# Revit family: Sanitary-Equipment_Urinal-Bill_085135
name_source: partatom
category: Plumbing Fixtures
revit_build: Autodesk Revit 2014 (Build: 20130308_1515(x64)
units: mm (PartAtom-declared; Revit-internal decimal feet)

## types (1)
- 085135 White Alpin
    BIMobject category = Urinals
    Depth (mm) = 355 mm
    Description = Urinal concealed inlet, syphonic action, vertical or horizontal outlet
    Drain Diameter (mm) = 50 mm  [stored 0.164042 ft]
    Edition number = 1
    Height (mm) = 510 mm  [stored 1.67323 ft]
    IFC Classification = Sanitary Terminal
    Installation instructions = http://pro.duravit.com
    Manufacturer = Duravit
    Manufacturer name = DURAVIT
    Masterformat 2014 Code = 22 41 13.16
    Masterformat 2014 Description = Residential Urinals
    Model = 085135
    NBS Reference Code = 31-93
    NBS Reference Description = Urinal And Wc Fittings
    Nominal height = 0 mm  [stored 0 ft]
    Nominal width = 350 mm  [stored 1.14829 ft]
    OmniClass Code = 23-31 21 00
    OmniClass Description = Urinals
    Option 01 = Options : model with fly
    Option 02 = Options : model without fly
    Primary Material = Ceramics-Duravit-White_Alpin
    Product Guid = f0090561-3040-4b8d-9a02-f5348f29c901
    Product SKU = urinals-urinal-bill-085135
    Product certification = http://pro.duravit.com
    Product data url = http://bimobject.com
    Product family = Urinals
    Product group = Urinal Bill
    QR code = http://bimobject.com
    Secondary Material = Chrome-Duravit
    Specification = 0851350000: Urinal Bill white concealed inlet 0851350007: Urinal Bill white concealed inlet, with fly 08513500001: Urinal Bill white concealed inlet, WonderGliss 08513500071: Urinal Bill white concealed inlet, with fly, WG
    Technical description = http://pro.duravit.com
    UNSPSC Code = 30181506
    URL = http://www.duravit.com
    Uniclass 1.4 Code = L721
    Uniclass 1.4 Description = Sanitary equipment
    Uniclass 2.0 Code = PR-31-93
    Uniclass 2.0 Description = Urinal And Wc Fittings
    Uniclass 2015 Code = Pr_40_20_93
    Uniclass 2015 Name = Urinal and WC fittings
    Uniformat II Code = D2010
    Uniformat II Description = Plumbing Fixtures
    Weight Net (Kg) = 12
    Width (mm) = 360 mm  [stored 1.1811 ft]

note: [stored X ft] marks values corroborated as IEEE doubles in the binary element streams (Revit-internal decimal feet)

## geometry (parser evidence)
native form markers: Sweep x6
no freeform markers — native parametric forms only
